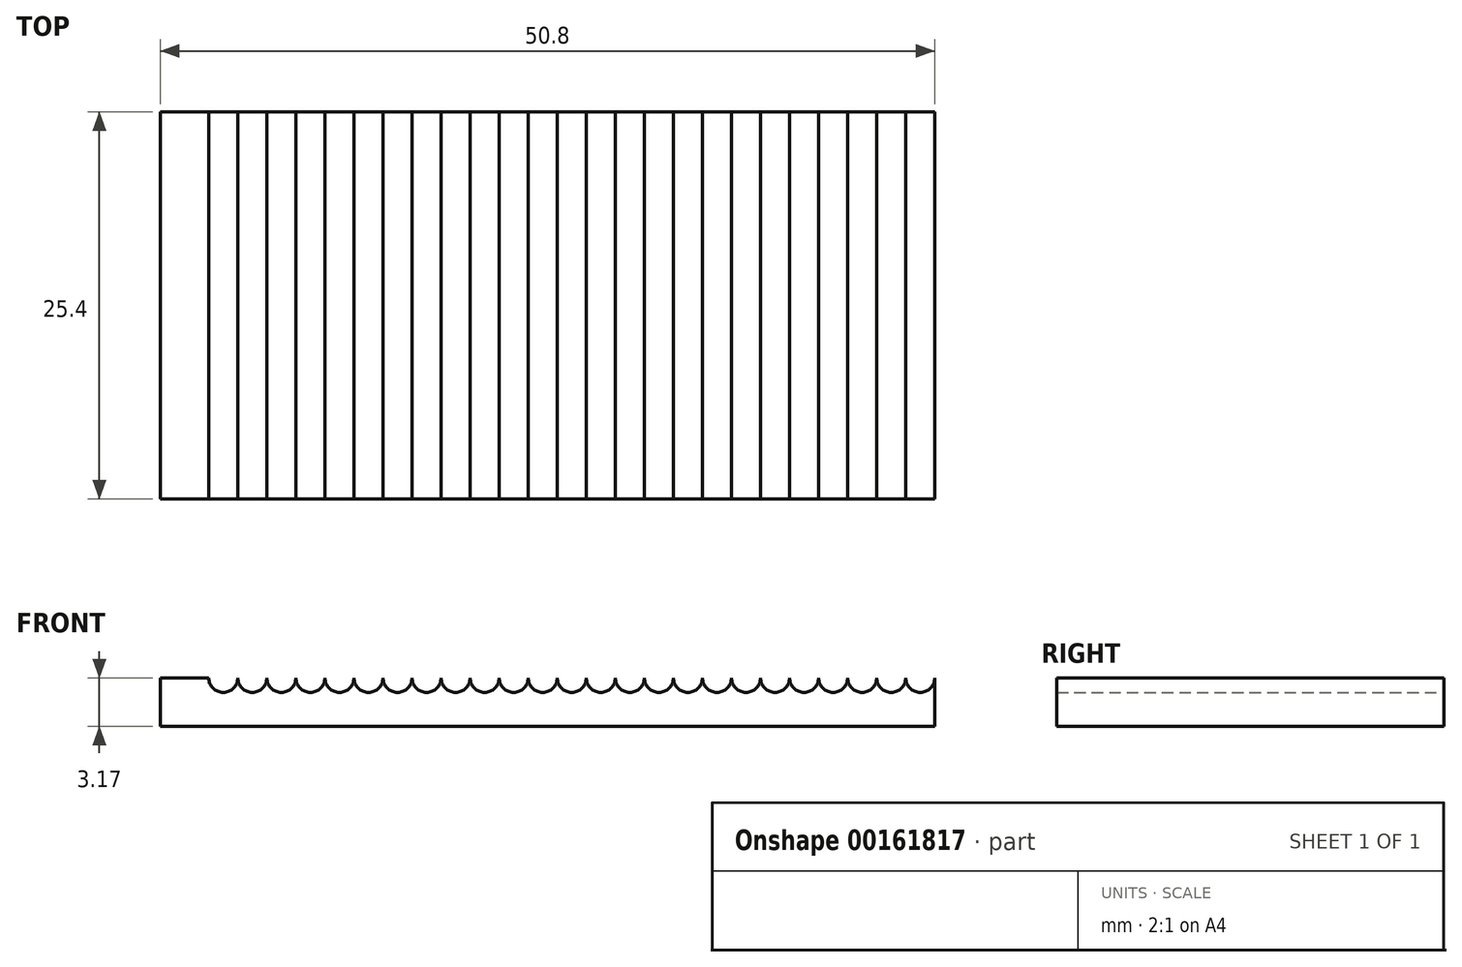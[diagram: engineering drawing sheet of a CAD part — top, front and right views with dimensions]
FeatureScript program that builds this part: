
annotation { "Feature Type Name" : "Feature", "Feature Type Description" : "" }
export const myFeature = defineFeature(function(context is Context, id is Id, definition is map)
    precondition{}
    {
        {
            var Q0;
            Q0=qCreatedBy(makeId("Front.planeOp"), FACE);
            var sketch = newSketch(context, id + "F0", { "sketchPlane" : qUnion([Q0])});
            skLineSegment(sketch, "E0", {"start": v(0, 0) * mm, "end": v(50.8, 0) * mm});
            skLineSegment(sketch, "E1", {"start": v(50.8, 0) * mm, "end": v(50.8, 3.17) * mm});
            skArc(sketch, "E2", {"start": v(48.9, 3.17) * mm, "mid": v(49.85, 2.22) * mm, "end": v(50.8, 3.17) * mm});
            skArc(sketch, "E3.1.0.0", {"start": v(47, 3.17) * mm, "mid": v(47.94, 2.22) * mm, "end": v(48.9, 3.17) * mm});
            skArc(sketch, "E3.2.0.0", {"start": v(45.09, 3.17) * mm, "mid": v(46.04, 2.22) * mm, "end": v(47, 3.17) * mm});
            skArc(sketch, "E3.3.0.0", {"start": v(43.18, 3.17) * mm, "mid": v(44.13, 2.22) * mm, "end": v(45.09, 3.17) * mm});
            skArc(sketch, "E3.4.0.0", {"start": v(41.28, 3.17) * mm, "mid": v(42.23, 2.22) * mm, "end": v(43.18, 3.17) * mm});
            skArc(sketch, "E3.5.0.0", {"start": v(39.37, 3.17) * mm, "mid": v(40.32, 2.22) * mm, "end": v(41.28, 3.17) * mm});
            skArc(sketch, "E3.6.0.0", {"start": v(37.47, 3.17) * mm, "mid": v(38.42, 2.22) * mm, "end": v(39.37, 3.17) * mm});
            skArc(sketch, "E3.7.0.0", {"start": v(35.56, 3.17) * mm, "mid": v(36.51, 2.22) * mm, "end": v(37.47, 3.17) * mm});
            skArc(sketch, "E3.8.0.0", {"start": v(33.66, 3.17) * mm, "mid": v(34.6, 2.22) * mm, "end": v(35.56, 3.17) * mm});
            skArc(sketch, "E3.9.0.0", {"start": v(31.75, 3.17) * mm, "mid": v(32.7, 2.22) * mm, "end": v(33.66, 3.17) * mm});
            skArc(sketch, "E3.10.0.0", {"start": v(29.85, 3.17) * mm, "mid": v(30.8, 2.22) * mm, "end": v(31.75, 3.17) * mm});
            skArc(sketch, "E3.11.0.0", {"start": v(27.94, 3.17) * mm, "mid": v(28.9, 2.22) * mm, "end": v(29.85, 3.17) * mm});
            skArc(sketch, "E3.12.0.0", {"start": v(26.04, 3.17) * mm, "mid": v(26.99, 2.22) * mm, "end": v(27.94, 3.17) * mm});
            skArc(sketch, "E3.13.0.0", {"start": v(24.13, 3.17) * mm, "mid": v(25.08, 2.22) * mm, "end": v(26.04, 3.17) * mm});
            skArc(sketch, "E3.14.0.0", {"start": v(22.23, 3.17) * mm, "mid": v(23.18, 2.22) * mm, "end": v(24.13, 3.17) * mm});
            skArc(sketch, "E3.15.0.0", {"start": v(20.32, 3.17) * mm, "mid": v(21.27, 2.22) * mm, "end": v(22.23, 3.17) * mm});
            skArc(sketch, "E3.16.0.0", {"start": v(18.42, 3.17) * mm, "mid": v(19.37, 2.22) * mm, "end": v(20.32, 3.17) * mm});
            skArc(sketch, "E3.17.0.0", {"start": v(16.51, 3.17) * mm, "mid": v(17.46, 2.22) * mm, "end": v(18.42, 3.17) * mm});
            skArc(sketch, "E3.18.0.0", {"start": v(14.6, 3.17) * mm, "mid": v(15.56, 2.22) * mm, "end": v(16.51, 3.17) * mm});
            skArc(sketch, "E3.19.0.0", {"start": v(12.7, 3.17) * mm, "mid": v(13.65, 2.22) * mm, "end": v(14.6, 3.17) * mm});
            skArc(sketch, "E3.20.0.0", {"start": v(10.8, 3.17) * mm, "mid": v(11.75, 2.22) * mm, "end": v(12.7, 3.17) * mm});
            skArc(sketch, "E3.21.0.0", {"start": v(8.9, 3.17) * mm, "mid": v(9.84, 2.22) * mm, "end": v(10.8, 3.17) * mm});
            skArc(sketch, "E3.22.0.0", {"start": v(6.99, 3.17) * mm, "mid": v(7.94, 2.22) * mm, "end": v(8.9, 3.17) * mm});
            skArc(sketch, "E3.23.0.0", {"start": v(5.08, 3.17) * mm, "mid": v(6.03, 2.22) * mm, "end": v(6.99, 3.17) * mm});
            skArc(sketch, "E3.24.0.0", {"start": v(3.18, 3.17) * mm, "mid": v(4.13, 2.22) * mm, "end": v(5.08, 3.17) * mm});
            skLineSegment(sketch, "E3.direction1", {"start": v(48.9, 3.17) * mm, "end": v(47, 3.17) * mm, "construction": true});
            skLineSegment(sketch, "E4", {"start": v(3.18, 3.17) * mm, "end": v(0, 3.17) * mm});
            skLineSegment(sketch, "E5", {"start": v(0, 3.17) * mm, "end": v(0, 0) * mm});
            skSolve(sketch);
        }
        {
            var Q0;
            Q0 = qSketchRegion(id + "F0", true);
            extrude(context, id + "F1", {"entities" : qUnion([Q0]), "depth" : 25.4 * mm, "offsetDistance" : 25.4 * mm});
        }
    });
